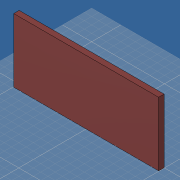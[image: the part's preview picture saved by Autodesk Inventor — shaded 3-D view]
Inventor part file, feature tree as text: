
AUTODESK INVENTOR PART (.ipt)
format: ipt  version: 2019 (Build 230136000, 136)  size: 96,768 bytes
history: native  units: mm
features: extrude x2, other x1, sketch x1
ambient origin geometry x8: Origin, YZ Plane, XZ Plane, XY Plane, X Axis, Y Axis, Z Axis, Center Point
bodies: Volumenkörper1 (feature_tree)
feature tree (4):
  other  "<userpath>\OneDrive\Dokumente\Inventor\Absauganlage\Absauganlage_Params.xlsx"
  sketch  "Skizze1"  dims[d0=175.0mm d1=398.0mm d2=8.0mm d3=17.0mm d4=17.0mm d5=15.0mm d6=0.0mm d7=6.0mm d8=0.0mm]
  extrude  "Extrusion1"  Depth=398.0mm
  extrude  "Extrusion2"  Depth=8.0mm
